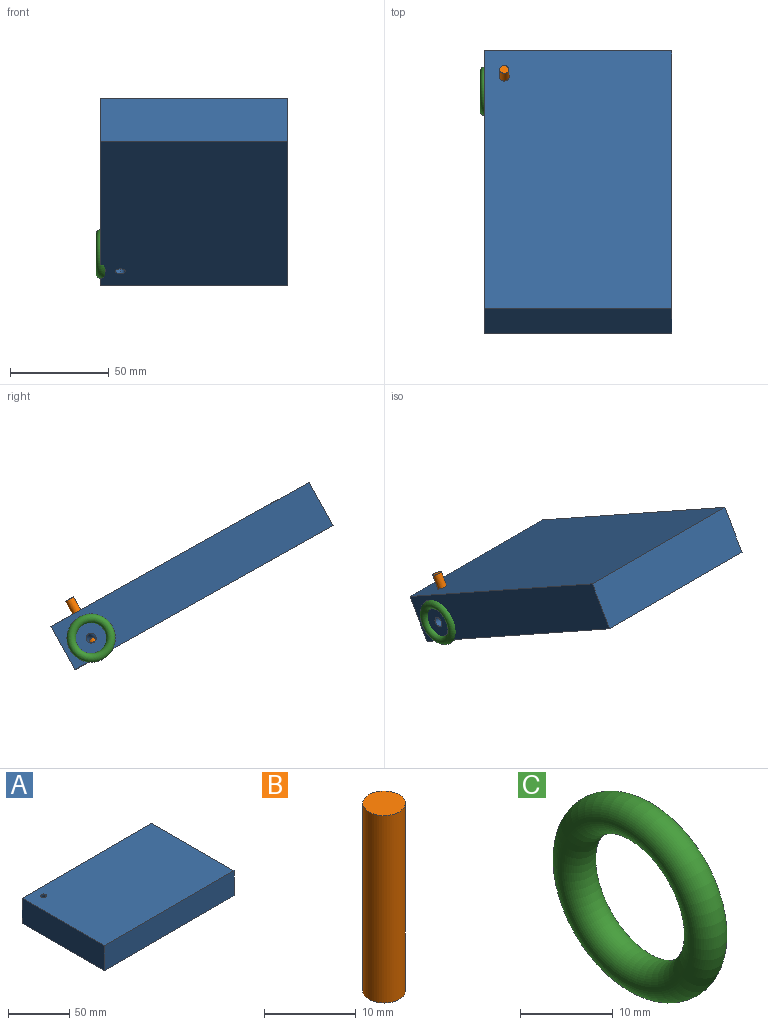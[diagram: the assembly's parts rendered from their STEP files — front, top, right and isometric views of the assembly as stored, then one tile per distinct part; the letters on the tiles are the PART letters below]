
ASSEMBLY  parts=3 mates=2
PART A: 8 faces, bbox 150x95x25 mm
  f0: cylinder r=2.5mm len=25mm, axis (0,0,-1), area 332.8mm2, adj f5,f6,f7
  f1: plane 150x25mm, normal (0,1,0), area 3730.4mm2, adj f2,f4,f5,f6,f7
  f2: plane 94.99x25mm, normal (-1,0,0), area 2374.8mm2, adj f1,f3,f5,f6
  f3: plane 150x25mm, normal (0,-1,0), area 3750mm2, adj f2,f4,f5,f6
  f4: plane 94.99x25mm, normal (1,0,0), area 2374.8mm2, adj f1,f3,f5,f6
  f5: plane 150x94.99mm, normal (0,0,1), area 14229.1mm2, adj f0,f1,f2,f3,f4,f7
  f6: plane 150x94.99mm, normal (0,0,-1), area 14229.1mm2, adj f0,f1,f2,f3,f4
  f7: torus R=10mm, axis (1,0,0), area 179.8mm2, adj f0,f1,f5
PART B: 3 faces, bbox 4.6x4.6x25 mm
  f0: cylinder r=2.32mm len=25mm, axis (0,0,1), area 365mm2, adj f1,f2
  f1: plane 4.65x4.65mm, normal (0,0,-1), area 17mm2, adj f0
  f2: plane 4.65x4.65mm, normal (0,0,1), area 17mm2, adj f0
PART C: 1 faces, bbox 4.6x26.6x26.6 mm
  f0: torus R=10mm, axis (-1,0,0), area 904.3mm2
PLACE A rot(axis=(0.7,-0.7,0.18),159.4deg) t=(-18.05,66.65,-4.4)mm
PLACE B rot(axis=(0.7,-0.7,0.18),159.4deg) t=(-18.05,58.16,-19.56)mm
PLACE C t=(-33.05,46.23,-35.16)mm fixed
MATE slider B.f0 <-> A.f0  axis (0,-0.49,-0.87) through (-8.05,45.07,-12.24)mm
MATE revolute A.f1 <-> C.f0  axis (-1,0,0) through (-18.05,46.23,-10.16)mm
